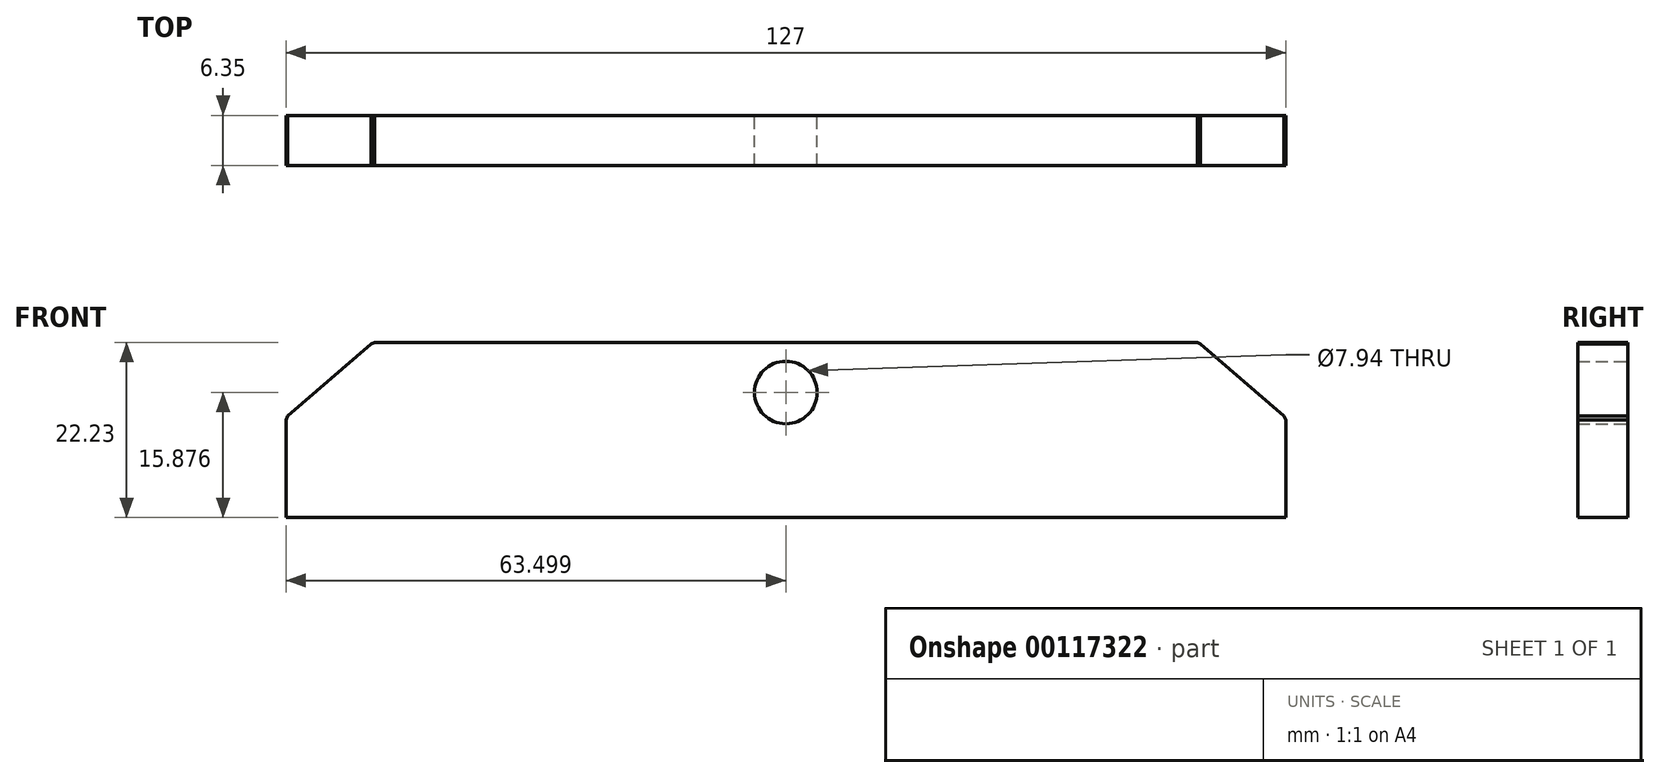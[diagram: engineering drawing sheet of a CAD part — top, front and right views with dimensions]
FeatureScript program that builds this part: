
annotation { "Feature Type Name" : "Feature", "Feature Type Description" : "" }
export const myFeature = defineFeature(function(context is Context, id is Id, definition is map)
    precondition{}
    {
        {
            var Q0;
            Q0=qCreatedBy(makeId("Front.planeOp"),FACE);
            var sketch = newSketch(context, id + "F0", { "sketchPlane" : qUnion([Q0])});
            skLineSegment(sketch, "E0.bottom", {"start": v(-72.8, -11.2) * mm, "end": v(32.2, -11.2) * mm});
            skLineSegment(sketch, "E0.top", {"start": v(-83.8, -33.43) * mm, "end": v(43.2, -33.43) * mm});
            skLineSegment(sketch, "E1", {"start": v(-80.13, -17.55) * mm, "end": v(39.53, -17.55) * mm, "construction": true});
            skLineSegment(sketch, "E2", {"start": v(-83.8, -20.73) * mm, "end": v(43.2, -20.73) * mm, "construction": true});
            skLineSegment(sketch, "E3", {"start": v(-83.8, -33.43) * mm, "end": v(-83.8, -20.73) * mm});
            skLineSegment(sketch, "E4", {"start": v(43.2, -33.43) * mm, "end": v(43.2, -20.73) * mm});
            skLineSegment(sketch, "E5", {"start": v(-72.8, -11.2) * mm, "end": v(-83.8, -20.73) * mm});
            skLineSegment(sketch, "E6", {"start": v(32.2, -11.2) * mm, "end": v(43.2, -20.73) * mm});
            skLineSegment(sketch, "E7", {"start": v(-20.3, -33.43) * mm, "end": v(-20.3, -11.2) * mm, "construction": true});
            skPoint(sketch, "E8", {"position": v(-20.3, -17.55) * mm});
            skSolve(sketch);
        }
        {
            var Q0;
            Q0=makeQuery(id+"F0.imprint","IMPRINT",FACE,{"disambiguationData":[TD([[makeQuery(id+"F0.imprint","IMPRINT",EDGE,{"derivedFrom":sQuery(id+"F0.wireOp",EDGE,"E0.bottom")}),-1.0]])]});
            extrude(context, id + "F1", {"entities" : qUnion([Q0]), "depth" : 6.35 * mm});
        }
        {
            var Q0;
            Q0=sQuery(id+"F0.wireOp",VERTEX,"E8");
            var Q1;
            Q1=makeQuery(id+"F1.opExtrude","SWEPT_BODY",BODY,{"disambiguationData":[OSD([sQuery(id+"F0.wireOp",EDGE,"E0.bottom"),sQuery(id+"F0.wireOp",EDGE,"E0.top"),sQuery(id+"F0.wireOp",EDGE,"VjLyuAZ2-bhlR-pRdG-ghIh-12mCt2n5kwmW"),sQuery(id+"F0.wireOp",EDGE,"td4jqYna-QlW0-usWU-RW3y-dBKkxZ3774Ke")])]});
            hole(context, id + "F2", {"style" : HoleStyle.SIMPLE, "endStyle" : HoleEndStyle.THROUGH, "oppositeDirection" : true, "standardTappedOrClearance" : lookupTablePath({ "standard" : "ANSI", "engagement" : "75%", "pitch" : "16 tpi", "size" : "3/8", "type" : "Tapped" }), "standardBlindInLast" : lookupTablePath({ "standard" : "ANSI", "engagement" : "75%", "pitch" : "16 tpi", "size" : "3/8", "type" : "Tapped" }), "holeDiameter" : 7.94 * mm, "locations" : qUnion([Q0]), "scope" : qUnion([Q1]), "isTappedThrough" : true, "majorDiameter" : 9.53 * mm, "showTappedDepth" : true});
        }
        {
            var Q0;
            Q0=makeQuery(id+"F1.opExtrude","SWEPT_EDGE",EDGE,{"disambiguationData":[OSD([sQuery(id+"F0.wireOp",EDGE,"E3"),sQuery(id+"F0.wireOp",EDGE,"E5")])]});
            var Q1;
            Q1=makeQuery(id+"F1.opExtrude","SWEPT_EDGE",EDGE,{"disambiguationData":[OSD([sQuery(id+"F0.wireOp",EDGE,"E0.bottom"),sQuery(id+"F0.wireOp",EDGE,"E5")])]});
            var Q2;
            Q2=makeQuery(id+"F1.opExtrude","SWEPT_EDGE",EDGE,{"disambiguationData":[OSD([sQuery(id+"F0.wireOp",EDGE,"E4"),sQuery(id+"F0.wireOp",EDGE,"E6")])]});
            var Q3;
            Q3=makeQuery(id+"F1.opExtrude","SWEPT_EDGE",EDGE,{"disambiguationData":[OSD([sQuery(id+"F0.wireOp",EDGE,"678c7640-2031-45e7-a4d3-9be44c7ccfa3.trimOffspring"),sQuery(id+"F0.wireOp",EDGE,"E6")])]});
            chamfer(context, id + "F3", {"entities" : qUnion([Q0, Q1, Q2, Q3]), "width" : 0.64 * mm, "tangentPropagation" : true});
        }
    });
